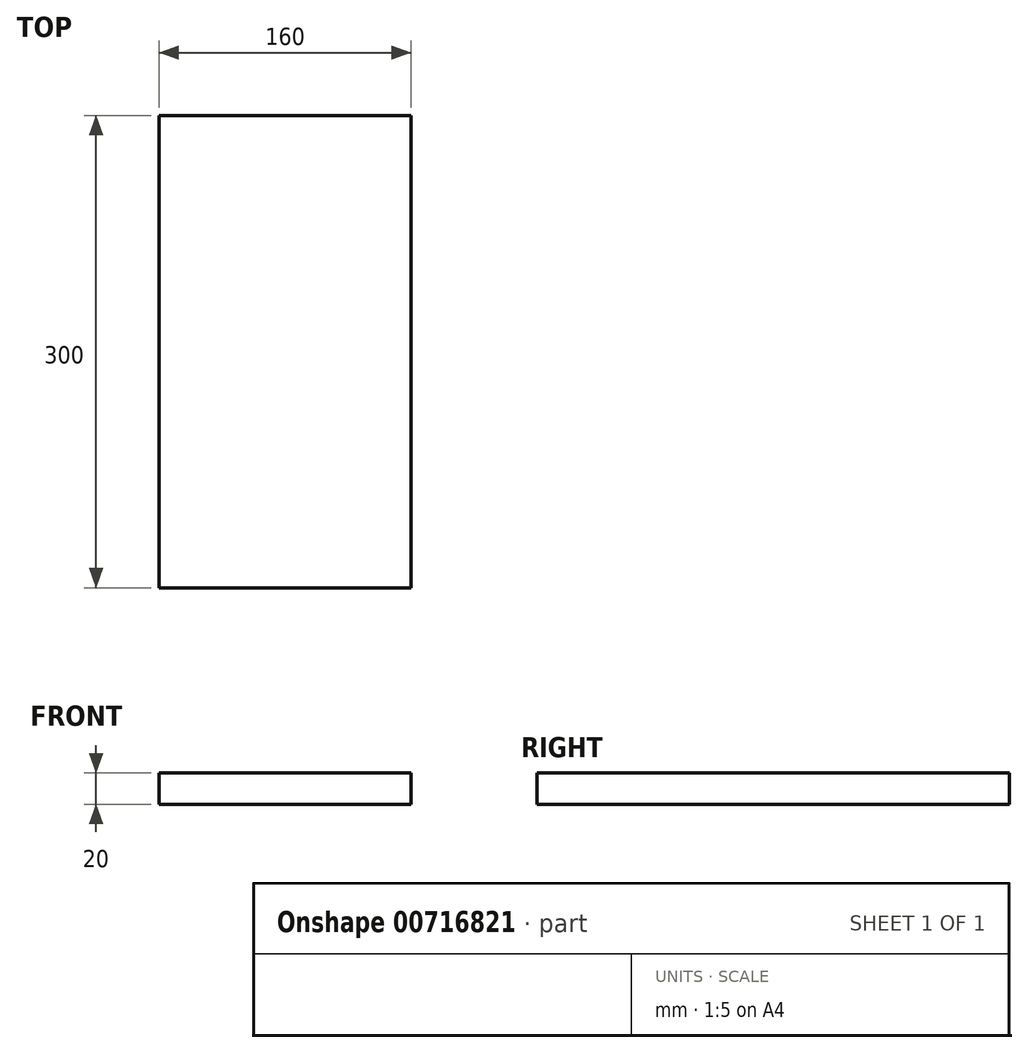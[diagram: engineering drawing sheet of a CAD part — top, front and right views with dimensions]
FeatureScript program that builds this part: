
annotation { "Feature Type Name" : "Feature", "Feature Type Description" : "" }
export const myFeature = defineFeature(function(context is Context, id is Id, definition is map)
    precondition{}
    {
        {
            var Q0;
            Q0=qCreatedBy(makeId("Front.planeOp"),FACE);
            var sketch = newSketch(context, id + "F0", { "sketchPlane" : qUnion([Q0])});
            skLineSegment(sketch, "E0.bottom", {"start": v(80, 10) * mm, "end": v(-80, 10) * mm});
            skLineSegment(sketch, "E0.top", {"start": v(80, -10) * mm, "end": v(-80, -10) * mm});
            skLineSegment(sketch, "E0.left", {"start": v(80, 10) * mm, "end": v(80, -10) * mm});
            skLineSegment(sketch, "E0.right", {"start": v(-80, 10) * mm, "end": v(-80, -10) * mm});
            skPoint(sketch, "E0.middle", {"position": v(0, 0) * mm});
            skSolve(sketch);
        }
        {
            var Q0;
            Q0 = qSketchRegion(id + "F0", true);
            extrude(context, id + "F1", {"entities" : qUnion([Q0]), "endBound" : BoundingType.SYMMETRIC, "depth" : 300 * mm, "offsetDistance" : 25 * mm});
        }
    });
